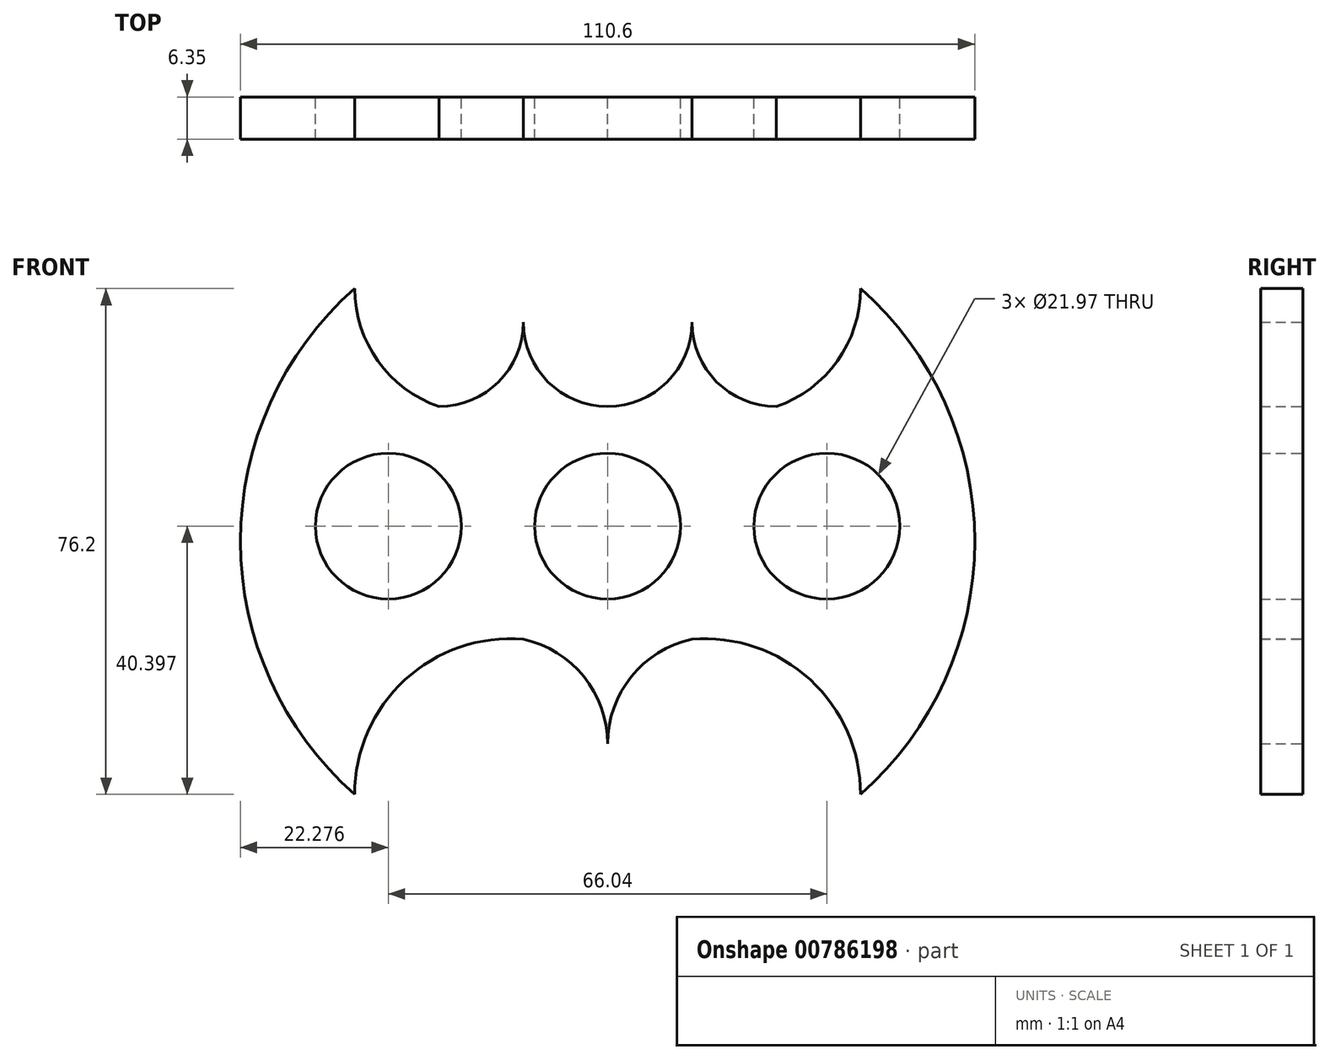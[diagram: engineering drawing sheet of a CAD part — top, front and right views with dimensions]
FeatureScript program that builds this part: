
annotation { "Feature Type Name" : "Feature", "Feature Type Description" : "" }
export const myFeature = defineFeature(function(context is Context, id is Id, definition is map)
    precondition{}
    {
        {
            var Q0;
            Q0=qCreatedBy(makeId("Front.planeOp"),FACE);
            var sketch = newSketch(context, id + "F0", { "sketchPlane" : qUnion([Q0])});
            skPoint(sketch, "E0.start.orphan", {"position": v(-9.63, -8.66) * mm});
            skArc(sketch, "E1", {"start": v(-35.03, 26.4) * mm, "mid": v(-26.05, 30.11) * mm, "end": v(-22.33, 39.1) * mm});
            skArc(sketch, "E2", {"start": v(3.07, 39.1) * mm, "mid": v(6.79, 30.11) * mm, "end": v(15.77, 26.4) * mm});
            skArc(sketch, "E3", {"start": v(-22.33, 39.1) * mm, "mid": v(-18.61, 30.11) * mm, "end": v(-9.63, 26.4) * mm});
            skArc(sketch, "E4", {"start": v(-9.63, 26.4) * mm, "mid": v(-0.65, 30.11) * mm, "end": v(3.07, 39.1) * mm});
            skArc(sketch, "E5", {"start": v(-47.73, 44.17) * mm, "mid": v(-64.93, 6.07) * mm, "end": v(-47.73, -32.03) * mm});
            skArc(sketch, "E6", {"start": v(28.47, -32.03) * mm, "mid": v(45.67, 6.07) * mm, "end": v(28.47, 44.17) * mm});
            skArc(sketch, "E7", {"start": v(-47.73, 44.17) * mm, "mid": v(-44.23, 33.25) * mm, "end": v(-35.03, 26.4) * mm});
            skArc(sketch, "E8", {"start": v(15.77, 26.4) * mm, "mid": v(24.97, 33.25) * mm, "end": v(28.47, 44.17) * mm});
            skArc(sketch, "E9", {"start": v(-22.33, -8.66) * mm, "mid": v(-40.16, -14.77) * mm, "end": v(-47.73, -32.03) * mm});
            skArc(sketch, "E10", {"start": v(28.47, -32.03) * mm, "mid": v(20.9, -14.77) * mm, "end": v(3.07, -8.66) * mm});
            skPoint(sketch, "E11.orphan", {"position": v(3.07, 26.4) * mm});
            skPoint(sketch, "E12.start.orphan", {"position": v(-22.33, 26.4) * mm});
            skArc(sketch, "E13", {"start": v(-9.63, -24.4) * mm, "mid": v(-13.2, -14.3) * mm, "end": v(-22.33, -8.66) * mm});
            skArc(sketch, "E14", {"start": v(3.07, -8.66) * mm, "mid": v(-6.06, -14.3) * mm, "end": v(-9.63, -24.4) * mm});
            skPoint(sketch, "E15.center.orphan", {"position": v(-9.63, 1) * mm});
            skPoint(sketch, "E16.end.orphan", {"position": v(0, 6.07) * mm});
            skCircle(sketch, "E17", {"center": v(-9.63, 8.37) * mm, "radius": 10.99 * mm});
            skLineSegment(sketch, "E18.trimOffspring", {"start": v(-9.63, 1) * mm, "end": v(-9.63, -2.62) * mm});
            skPoint(sketch, "E19.start.orphan", {"position": v(-64.88, 8.37) * mm});
            skPoint(sketch, "E20.trimOffspring.end.orphan", {"position": v(45.61, 8.37) * mm});
            skCircle(sketch, "E21", {"center": v(-42.65, 8.37) * mm, "radius": 10.99 * mm});
            skCircle(sketch, "E22", {"center": v(23.39, 8.37) * mm, "radius": 10.99 * mm});
            skSolve(sketch);
        }
        {
            var Q0;
            Q0=qSketchRegion(id+"F0",true);
            extrude(context, id + "F1", {"entities" : qUnion([Q0]), "depth" : 6.35 * mm, "offsetDistance" : 25.4 * mm});
        }
    });
